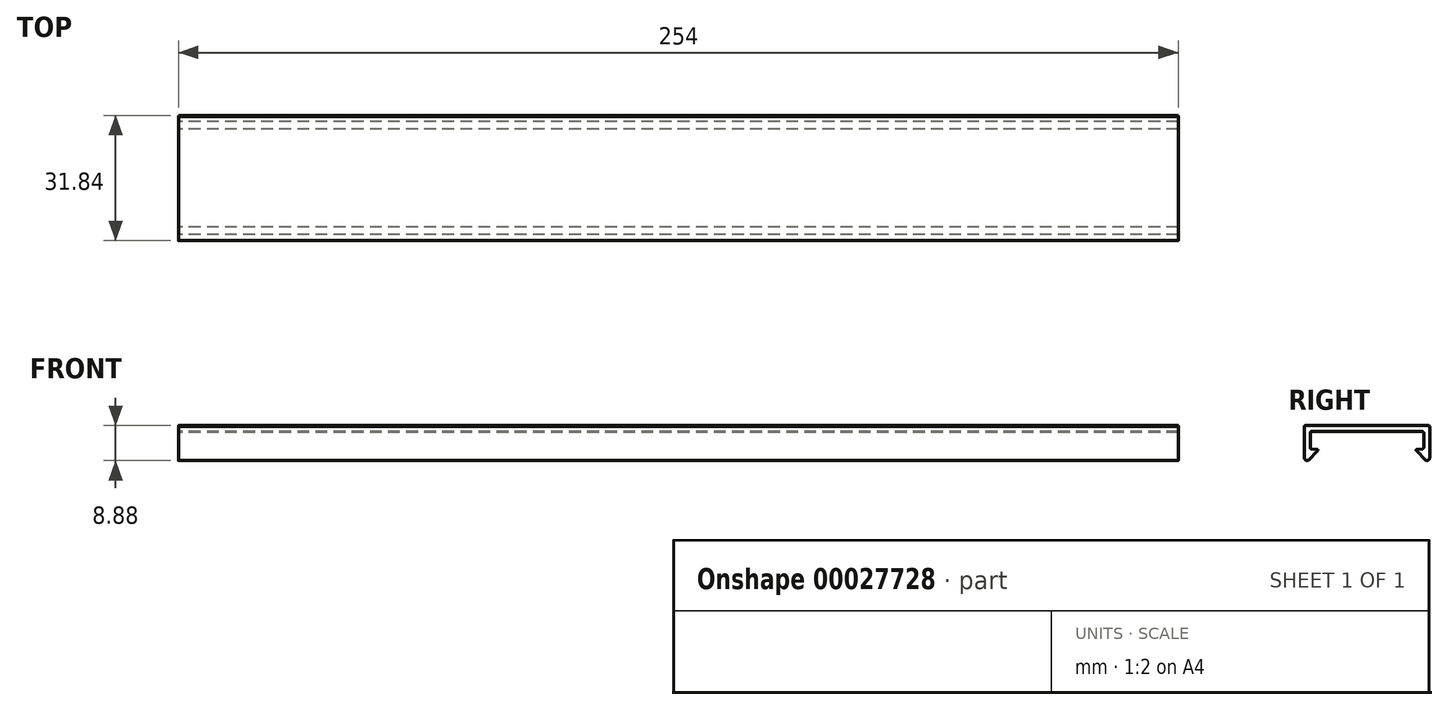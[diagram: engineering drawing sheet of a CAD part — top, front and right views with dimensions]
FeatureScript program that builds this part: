
annotation { "Feature Type Name" : "Feature", "Feature Type Description" : "" }
export const myFeature = defineFeature(function(context is Context, id is Id, definition is map)
    precondition{}
    {
        {
            var Q0;
            Q0=qCreatedBy(makeId("Right.planeOp"),FACE);
            var sketch = newSketch(context, id + "F0", { "sketchPlane" : qUnion([Q0])});
            skLineSegment(sketch, "E0", {"start": v(12.57, -1.64) * mm, "end": v(14.18, -1.43) * mm});
            skArc(sketch, "E1", {"start": v(14.18, -1.43) * mm, "mid": v(14.34, -1.35) * mm, "end": v(14.4, -1.18) * mm});
            skLineSegment(sketch, "E2", {"start": v(14.4, -1.18) * mm, "end": v(14.4, 2.66) * mm});
            skArc(sketch, "E3", {"start": v(14.4, 2.66) * mm, "mid": v(14.33, 2.84) * mm, "end": v(14.15, 2.91) * mm});
            skLineSegment(sketch, "E4", {"start": v(14.15, 2.91) * mm, "end": v(-14.15, 2.91) * mm});
            skArc(sketch, "E5", {"start": v(-14.15, 2.91) * mm, "mid": v(-14.33, 2.84) * mm, "end": v(-14.4, 2.66) * mm});
            skLineSegment(sketch, "E6", {"start": v(-14.4, 2.66) * mm, "end": v(-14.4, -1.18) * mm});
            skArc(sketch, "E7", {"start": v(-14.4, -1.18) * mm, "mid": v(-14.34, -1.35) * mm, "end": v(-14.18, -1.43) * mm});
            skLineSegment(sketch, "E8", {"start": v(-14.18, -1.43) * mm, "end": v(-12.57, -1.64) * mm});
            skArc(sketch, "E9", {"start": v(-12.57, -1.64) * mm, "mid": v(-12.47, -1.73) * mm, "end": v(-12.5, -1.86) * mm});
            skLineSegment(sketch, "E10", {"start": v(-12.5, -1.86) * mm, "end": v(-14.94, -4.36) * mm});
            skArc(sketch, "E11", {"start": v(-14.94, -4.36) * mm, "mid": v(-15.02, -4.41) * mm, "end": v(-15.1, -4.43) * mm});
            skArc(sketch, "E12", {"start": v(-15.1, -4.43) * mm, "mid": v(-15.68, -4.24) * mm, "end": v(-15.92, -3.69) * mm});
            skLineSegment(sketch, "E13", {"start": v(-15.92, -3.69) * mm, "end": v(-15.92, 4.18) * mm});
            skArc(sketch, "E14", {"start": v(-15.92, 4.18) * mm, "mid": v(-15.85, 4.36) * mm, "end": v(-15.67, 4.44) * mm});
            skLineSegment(sketch, "E15", {"start": v(-15.67, 4.44) * mm, "end": v(15.67, 4.44) * mm});
            skLineSegment(sketch, "E16", {"start": v(15.67, 4.44) * mm, "end": v(15.85, 4.36) * mm});
            skLineSegment(sketch, "E17", {"start": v(15.85, 4.36) * mm, "end": v(15.92, 4.18) * mm});
            skLineSegment(sketch, "E18", {"start": v(15.92, 4.18) * mm, "end": v(15.92, -3.69) * mm});
            skArc(sketch, "E19", {"start": v(15.92, -3.69) * mm, "mid": v(15.68, -4.24) * mm, "end": v(15.1, -4.43) * mm});
            skArc(sketch, "E20", {"start": v(15.1, -4.43) * mm, "mid": v(15.02, -4.41) * mm, "end": v(14.94, -4.36) * mm});
            skLineSegment(sketch, "E21", {"start": v(14.94, -4.36) * mm, "end": v(12.5, -1.86) * mm});
            skArc(sketch, "E22", {"start": v(12.5, -1.86) * mm, "mid": v(12.47, -1.73) * mm, "end": v(12.57, -1.64) * mm});
            skSolve(sketch);
        }
        {
            var Q0;
            Q0=qSketchRegion(id+"F0",true);
            extrude(context, id + "F1", {"entities" : qUnion([Q0]), "endBound" : BoundingType.SYMMETRIC, "depth" : 254 * mm});
        }
    });
